# Revit family: M_Level Valve - 15-50 mm - Threaded
name_source: partatom
category: Pipe Accessories
revit_build: Autodesk Revit 2014 (Build: 20130308_1515(x64)
units: mm (PartAtom-declared; Revit-internal decimal feet)

## types (6) — shared parameters
Valve Material = PVC, Green

## per-type parameters (varying)
| type | Body Diameter | Body Radius | Bonnet Diameter | Bonnet Radius | Bottom Radius | H2 | H3 | Height 1 | Height 2 | K Coefficient | Nominal Radius | Outside Diameter | Outside Radius | Radius 1 | Socket Diameter | Socket Radius | Socket Thickness | Valve Length |
| 15 mm | 78 mm | 39 mm | 72 mm | 36 mm | 34 mm | 83 mm | 25 mm  [stored 0.082021 ft] | 67 mm | 97 mm  [stored 0.318241 ft] | 1.17 | 8 mm | 38 mm | 19 mm | 12 mm  [stored 0.0393701 ft] | 46 mm | 23 mm | 9 mm  [stored 0.0295276 ft] | 124 mm |
| 50 mm | 103 mm | 52 mm | 97 mm  [stored 0.318241 ft] | 49 mm | 45 mm | 110 mm  [stored 0.360892 ft] | 33 mm | 87 mm  [stored 0.285433 ft] | 120 mm  [stored 0.393701 ft] | 8.9 | 25 mm | 70 mm | 35 mm | 16 mm  [stored 0.0524934 ft] | 84 mm | 42 mm | 16 mm  [stored 0.0524934 ft] | 165 mm |
| 25 mm | 78 mm | 39 mm | 72 mm | 36 mm | 34 mm | 83 mm | 25 mm  [stored 0.082021 ft] | 67 mm | 97 mm  [stored 0.318241 ft] | 8.9 | 13 mm | 38 mm | 19 mm | 12 mm  [stored 0.0393701 ft] | 46 mm | 23 mm | 9 mm  [stored 0.0295276 ft] | 124 mm |
| 32 mm | 91 mm | 46 mm | 85 mm | 43 mm | 40 mm  [stored 0.131234 ft] | 97 mm  [stored 0.318241 ft] | 29 mm | 80 mm  [stored 0.262467 ft] | 106 mm  [stored 0.347769 ft] | 6.02 | 16 mm | 64 mm | 32 mm  [stored 0.104987 ft] | 14 mm  [stored 0.0459318 ft] | 76 mm | 38 mm | 14 mm  [stored 0.0459318 ft] | 146 mm |
| 40 mm | 91 mm | 46 mm | 85 mm | 43 mm | 40 mm  [stored 0.131234 ft] | 97 mm  [stored 0.318241 ft] | 29 mm | 80 mm  [stored 0.262467 ft] | 106 mm  [stored 0.347769 ft] | 7.21 | 20 mm | 64 mm | 32 mm  [stored 0.104987 ft] | 14 mm  [stored 0.0459318 ft] | 76 mm | 38 mm | 14 mm  [stored 0.0459318 ft] | 146 mm |
| 20 mm | 78 mm | 39 mm | 72 mm | 36 mm | 34 mm | 83 mm | 25 mm  [stored 0.082021 ft] | 67 mm | 97 mm  [stored 0.318241 ft] | 4.75 | 10 mm | 38 mm | 19 mm | 12 mm  [stored 0.0393701 ft] | 46 mm | 23 mm | 9 mm  [stored 0.0295276 ft] | 124 mm |

note: column(s) folded — value = type name in every type: Nominal Diameter

note: [stored X ft] marks values corroborated as IEEE doubles in the binary element streams (Revit-internal decimal feet)

## geometry (parser evidence)
native form markers: Blend x2, Sweep x3
no freeform markers — native parametric forms only
